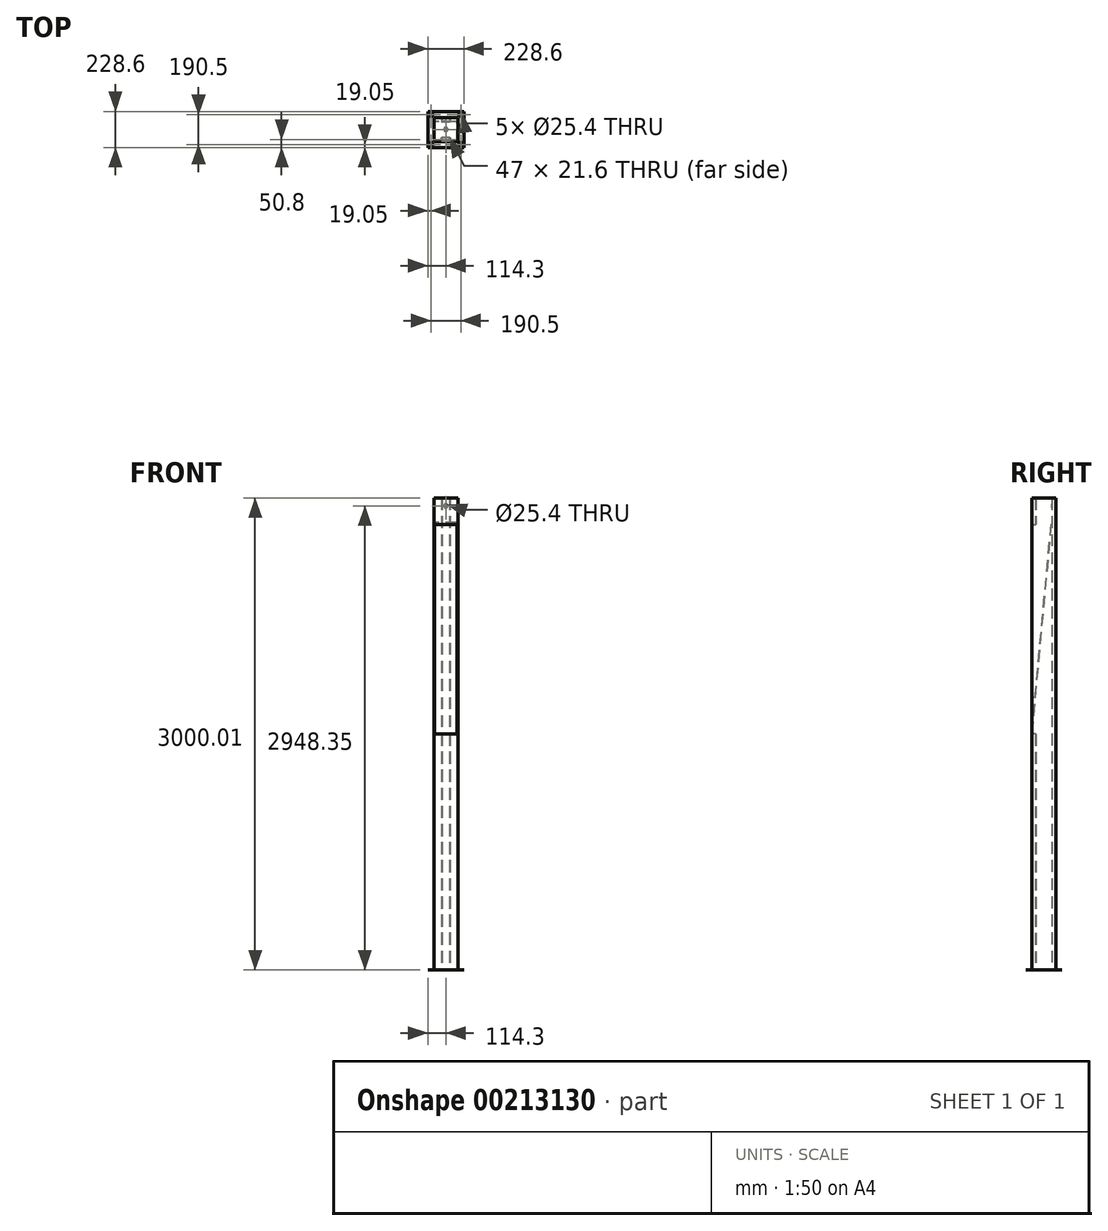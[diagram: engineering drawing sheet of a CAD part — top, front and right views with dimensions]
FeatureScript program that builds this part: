
annotation { "Feature Type Name" : "Feature", "Feature Type Description" : "" }
export const myFeature = defineFeature(function(context is Context, id is Id, definition is map)
    precondition{}
    {
        {
            var Q0;
            Q0=qCreatedBy(makeId("Top.planeOp"),FACE);
            var sketch = newSketch(context, id + "F0", { "sketchPlane" : qUnion([Q0])});
            skPoint(sketch, "E0.middle", {"position": v(0, 0) * mm});
            skLineSegment(sketch, "E1", {"start": v(-76.2, 76.2) * mm, "end": v(-25.4, 76.2) * mm});
            skLineSegment(sketch, "E2", {"start": v(-25.4, 76.2) * mm, "end": v(-25.4, 50.8) * mm});
            skLineSegment(sketch, "E3.MirrorCS", {"start": v(-25.4, -76.2) * mm, "end": v(-25.4, -50.8) * mm});
            skLineSegment(sketch, "E4.MirrorCS", {"start": v(-76.2, -76.2) * mm, "end": v(-25.4, -76.2) * mm});
            skLineSegment(sketch, "E5.0", {"start": v(-27.3, -74.3) * mm, "end": v(-27.3, -50.8) * mm});
            skLineSegment(sketch, "E5.1", {"start": v(-27.3, 74.3) * mm, "end": v(-27.3, 50.8) * mm});
            skLineSegment(sketch, "E5.2", {"start": v(-74.3, 74.3) * mm, "end": v(-27.3, 74.3) * mm});
            skLineSegment(sketch, "E5.3", {"start": v(-74.3, 74.3) * mm, "end": v(-74.3, -74.3) * mm});
            skLineSegment(sketch, "E5.4", {"start": v(-74.3, -74.3) * mm, "end": v(-27.3, -74.3) * mm});
            skLineSegment(sketch, "E6", {"start": v(-27.3, 50.8) * mm, "end": v(-25.4, 50.8) * mm});
            skLineSegment(sketch, "E7", {"start": v(-27.3, -50.8) * mm, "end": v(-25.4, -50.8) * mm});
            skLineSegment(sketch, "E8", {"start": v(-76.2, 76.2) * mm, "end": v(-76.2, -76.2) * mm});
            skLineSegment(sketch, "E9.MirrorCS", {"start": v(25.4, 76.2) * mm, "end": v(25.4, 50.8) * mm});
            skLineSegment(sketch, "E10.MirrorCS", {"start": v(27.3, 74.3) * mm, "end": v(27.3, 50.8) * mm});
            skLineSegment(sketch, "E11.MirrorCS", {"start": v(74.3, 74.3) * mm, "end": v(27.3, 74.3) * mm});
            skLineSegment(sketch, "E12.MirrorCS", {"start": v(74.3, 74.3) * mm, "end": v(74.3, -74.3) * mm});
            skLineSegment(sketch, "E13.MirrorCS", {"start": v(74.3, -74.3) * mm, "end": v(27.3, -74.3) * mm});
            skLineSegment(sketch, "E14.MirrorCS", {"start": v(27.3, -74.3) * mm, "end": v(27.3, -50.8) * mm});
            skLineSegment(sketch, "E15.MirrorCS", {"start": v(25.4, -76.2) * mm, "end": v(25.4, -50.8) * mm});
            skLineSegment(sketch, "E16.MirrorCS", {"start": v(27.3, -50.8) * mm, "end": v(25.4, -50.8) * mm});
            skLineSegment(sketch, "E17.MirrorCS", {"start": v(27.3, 50.8) * mm, "end": v(25.4, 50.8) * mm});
            skLineSegment(sketch, "E18", {"start": v(25.4, -76.2) * mm, "end": v(76.2, -76.2) * mm});
            skLineSegment(sketch, "E19", {"start": v(76.2, -76.2) * mm, "end": v(76.2, 76.2) * mm});
            skLineSegment(sketch, "E20", {"start": v(25.4, 76.2) * mm, "end": v(76.2, 76.2) * mm});
            skLineSegment(sketch, "E21", {"start": v(-25.4, 76.2) * mm, "end": v(25.4, 76.2) * mm});
            skLineSegment(sketch, "E22", {"start": v(-25.4, 50.8) * mm, "end": v(25.4, 50.8) * mm});
            skLineSegment(sketch, "E23.0", {"start": v(-23.5, 74.3) * mm, "end": v(23.5, 74.3) * mm});
            skLineSegment(sketch, "E23.1", {"start": v(-23.5, 74.3) * mm, "end": v(-23.5, 52.7) * mm});
            skLineSegment(sketch, "E23.2", {"start": v(-23.5, 52.7) * mm, "end": v(23.5, 52.7) * mm});
            skLineSegment(sketch, "E23.3", {"start": v(23.5, 74.3) * mm, "end": v(23.5, 52.7) * mm});
            skLineSegment(sketch, "E24.MirrorCS", {"start": v(-25.4, -50.8) * mm, "end": v(25.4, -50.8) * mm});
            skLineSegment(sketch, "E25.MirrorCS", {"start": v(-23.5, -52.7) * mm, "end": v(23.5, -52.7) * mm});
            skLineSegment(sketch, "E26.MirrorCS", {"start": v(-23.5, -74.3) * mm, "end": v(-23.5, -52.7) * mm});
            skLineSegment(sketch, "E27.MirrorCS", {"start": v(-23.5, -74.3) * mm, "end": v(23.5, -74.3) * mm});
            skLineSegment(sketch, "E28.MirrorCS", {"start": v(23.5, -74.3) * mm, "end": v(23.5, -52.7) * mm});
            skLineSegment(sketch, "E29.MirrorCS", {"start": v(-25.4, -76.2) * mm, "end": v(25.4, -76.2) * mm});
            skSolve(sketch);
        }
        {
            var Q0;
            Q0=makeQuery(id+"F0.imprint","IMPRINT",FACE,{"disambiguationData":[TD([[makeQuery(id+"F0.imprint","IMPRINT",EDGE,{"derivedFrom":sQuery(id+"F0.wireOp",EDGE,"E3.MirrorCS")}),-1.0]])]});
            var Q1;
            Q1=makeQuery(id+"F0.imprint","IMPRINT",FACE,{"disambiguationData":[TD([[makeQuery(id+"F0.imprint","IMPRINT",EDGE,{"derivedFrom":sQuery(id+"F0.wireOp",EDGE,"E2")}),1.0]])]});
            var Q2;
            Q2=makeQuery(id+"F0.imprint","IMPRINT",FACE,{"disambiguationData":[TD([[makeQuery(id+"F0.imprint","IMPRINT",EDGE,{"derivedFrom":sQuery(id+"F0.wireOp",EDGE,"E1")}),-1.0]])]});
            var Q3;
            Q3=makeQuery(id+"F0.imprint","IMPRINT",FACE,{"disambiguationData":[TD([[makeQuery(id+"F0.imprint","IMPRINT",EDGE,{"derivedFrom":sQuery(id+"F0.wireOp",EDGE,"E10.MirrorCS")}),-1.0]])]});
            extrude(context, id + "F1", {"entities" : qUnion([Q0, Q1, Q2, Q3]), "endBound" : BoundingType.SYMMETRIC, "depth" : 3000 * mm});
        }
        {
            var Q0;
            Q0=makeQuery(id+"F1.opExtrude","CAP_FACE",FACE,{"disambiguationData":[OSD([sQuery(id+"F0.wireOp",EDGE,"E1"),sQuery(id+"F0.wireOp",EDGE,"E4.MirrorCS"),sQuery(id+"F0.wireOp",EDGE,"E5.0"),sQuery(id+"F0.wireOp",EDGE,"E5.1"),sQuery(id+"F0.wireOp",EDGE,"E5.2"),sQuery(id+"F0.wireOp",EDGE,"E5.3"),sQuery(id+"F0.wireOp",EDGE,"E5.4"),sQuery(id+"F0.wireOp",EDGE,"E6"),sQuery(id+"F0.wireOp",EDGE,"E7"),sQuery(id+"F0.wireOp",EDGE,"E8"),sQuery(id+"F0.wireOp",EDGE,"E10.MirrorCS"),sQuery(id+"F0.wireOp",EDGE,"E11.MirrorCS"),sQuery(id+"F0.wireOp",EDGE,"E12.MirrorCS"),sQuery(id+"F0.wireOp",EDGE,"E13.MirrorCS"),sQuery(id+"F0.wireOp",EDGE,"E14.MirrorCS"),sQuery(id+"F0.wireOp",EDGE,"E16.MirrorCS"),sQuery(id+"F0.wireOp",EDGE,"E17.MirrorCS"),sQuery(id+"F0.wireOp",EDGE,"E18"),sQuery(id+"F0.wireOp",EDGE,"E19"),sQuery(id+"F0.wireOp",EDGE,"E20"),sQuery(id+"F0.wireOp",EDGE,"E21"),sQuery(id+"F0.wireOp",EDGE,"E22"),sQuery(id+"F0.wireOp",EDGE,"E23.0"),sQuery(id+"F0.wireOp",EDGE,"E23.1"),sQuery(id+"F0.wireOp",EDGE,"E23.2"),sQuery(id+"F0.wireOp",EDGE,"E23.3"),sQuery(id+"F0.wireOp",EDGE,"E24.MirrorCS"),sQuery(id+"F0.wireOp",EDGE,"E25.MirrorCS"),sQuery(id+"F0.wireOp",EDGE,"E26.MirrorCS"),sQuery(id+"F0.wireOp",EDGE,"E27.MirrorCS"),sQuery(id+"F0.wireOp",EDGE,"E28.MirrorCS"),sQuery(id+"F0.wireOp",EDGE,"E29.MirrorCS")])],"isStart":true});
            var sketch = newSketch(context, id + "F2", { "sketchPlane" : qUnion([Q0])});
            skLineSegment(sketch, "E30.bottom", {"start": v(-114.3, 114.3) * mm, "end": v(114.3, 114.3) * mm});
            skLineSegment(sketch, "E30.top", {"start": v(-114.3, -114.3) * mm, "end": v(114.3, -114.3) * mm});
            skLineSegment(sketch, "E30.left", {"start": v(-114.3, 114.3) * mm, "end": v(-114.3, -114.3) * mm});
            skLineSegment(sketch, "E30.right", {"start": v(114.3, 114.3) * mm, "end": v(114.3, -114.3) * mm});
            skPoint(sketch, "E30.middle", {"position": v(0, 0) * mm});
            skLineSegment(sketch, "E31", {"start": v(-114.3, 114.3) * mm, "end": v(-76.2, 76.2) * mm, "construction": true});
            skCircle(sketch, "E32", {"center": v(-95.25, 95.25) * mm, "radius": 12.7 * mm});
            skCircle(sketch, "E33.MirrorC", {"center": v(-95.25, -95.25) * mm, "radius": 12.7 * mm});
            skCircle(sketch, "E34.MirrorC", {"center": v(95.25, 95.25) * mm, "radius": 12.7 * mm});
            skCircle(sketch, "E35.MirrorC", {"center": v(95.25, -95.25) * mm, "radius": 12.7 * mm});
            skCircle(sketch, "E36", {"center": v(0, 0) * mm, "radius": 12.7 * mm});
            skLineSegment(sketch, "E37.bottom", {"start": v(-95.25, -95.25) * mm, "end": v(95.25, -95.25) * mm, "construction": true});
            skLineSegment(sketch, "E37.top", {"start": v(-95.25, 95.25) * mm, "end": v(95.25, 95.25) * mm, "construction": true});
            skLineSegment(sketch, "E37.left", {"start": v(-95.25, -95.25) * mm, "end": v(-95.25, 95.25) * mm, "construction": true});
            skLineSegment(sketch, "E37.right", {"start": v(95.25, -95.25) * mm, "end": v(95.25, 95.25) * mm, "construction": true});
            skSolve(sketch);
        }
        {
            var Q0;
            Q0 = qSketchRegion(id + "F2", true);
            extrude(context, id + "F3", {"entities" : qUnion([Q0]), "depth" : 3 / 203.2 * mm});
        }
        {
            var Q0;
            Q0=makeQuery(id+"F1.opExtrude","SWEPT_FACE",FACE,{"disambiguationData":[OSD([sQuery(id+"F0.wireOp",EDGE,"E4.MirrorCS"),sQuery(id+"F0.wireOp",EDGE,"E18"),sQuery(id+"F0.wireOp",EDGE,"E29.MirrorCS")])]});
            var sketch = newSketch(context, id + "F4", { "sketchPlane" : qUnion([Q0])});
            skLineSegment(sketch, "E38", {"start": v(0, 1500) * mm, "end": v(0, 1330) * mm, "construction": true});
            skPoint(sketch, "E38.endSnap0", {"position": v(0, 1500) * mm});
            skLineSegment(sketch, "E39.bottom", {"start": v(72.28, 1330) * mm, "end": v(-72.28, 1330) * mm});
            skLineSegment(sketch, "E39.left", {"start": v(72.28, 1330) * mm, "end": v(72.28, 0) * mm});
            skLineSegment(sketch, "E39.right", {"start": v(-72.28, 1330) * mm, "end": v(-72.28, 0) * mm});
            skPoint(sketch, "E39.middle", {"position": v(0, 0) * mm});
            skLineSegment(sketch, "E40", {"start": v(-72.28, 0) * mm, "end": v(72.28, 0) * mm});
            skPoint(sketch, "E39.top.end.orphan", {"position": v(-72.28, -1330) * mm});
            skPoint(sketch, "E39.top.start.orphan", {"position": v(72.28, -1330) * mm});
            skPoint(sketch, "E41.orphan", {"position": v(76.2, 0) * mm});
            skSolve(sketch);
        }
        {
            var Q0;
            Q0=makeQuery(id+"F4.imprint","IMPRINT",FACE,{"disambiguationData":[TD([[makeQuery(id+"F4.imprint","IMPRINT",EDGE,{"derivedFrom":sQuery(id+"F4.wireOp",EDGE,"E39.bottom")}),1.0]])]});
            extrude(context, id + "F5", {"entities" : qUnion([Q0]), "operationType" : NewBodyOperationType.REMOVE, "oppositeDirection" : true, "depth" : 81 * mm});
        }
        {
            var Q0;
            Q0=makeQuery(id+"F1.opExtrude","CAP_FACE",FACE,{"disambiguationData":[OSD([sQuery(id+"F0.wireOp",EDGE,"E1"),sQuery(id+"F0.wireOp",EDGE,"E4.MirrorCS"),sQuery(id+"F0.wireOp",EDGE,"E5.0"),sQuery(id+"F0.wireOp",EDGE,"E5.1"),sQuery(id+"F0.wireOp",EDGE,"E5.2"),sQuery(id+"F0.wireOp",EDGE,"E5.3"),sQuery(id+"F0.wireOp",EDGE,"E5.4"),sQuery(id+"F0.wireOp",EDGE,"E6"),sQuery(id+"F0.wireOp",EDGE,"E7"),sQuery(id+"F0.wireOp",EDGE,"E8"),sQuery(id+"F0.wireOp",EDGE,"E10.MirrorCS"),sQuery(id+"F0.wireOp",EDGE,"E11.MirrorCS"),sQuery(id+"F0.wireOp",EDGE,"E12.MirrorCS"),sQuery(id+"F0.wireOp",EDGE,"E13.MirrorCS"),sQuery(id+"F0.wireOp",EDGE,"E14.MirrorCS"),sQuery(id+"F0.wireOp",EDGE,"E16.MirrorCS"),sQuery(id+"F0.wireOp",EDGE,"E17.MirrorCS"),sQuery(id+"F0.wireOp",EDGE,"E18"),sQuery(id+"F0.wireOp",EDGE,"E19"),sQuery(id+"F0.wireOp",EDGE,"E20"),sQuery(id+"F0.wireOp",EDGE,"E21"),sQuery(id+"F0.wireOp",EDGE,"E22"),sQuery(id+"F0.wireOp",EDGE,"E23.0"),sQuery(id+"F0.wireOp",EDGE,"E23.1"),sQuery(id+"F0.wireOp",EDGE,"E23.2"),sQuery(id+"F0.wireOp",EDGE,"E23.3"),sQuery(id+"F0.wireOp",EDGE,"E24.MirrorCS"),sQuery(id+"F0.wireOp",EDGE,"E25.MirrorCS"),sQuery(id+"F0.wireOp",EDGE,"E26.MirrorCS"),sQuery(id+"F0.wireOp",EDGE,"E27.MirrorCS"),sQuery(id+"F0.wireOp",EDGE,"E28.MirrorCS"),sQuery(id+"F0.wireOp",EDGE,"E29.MirrorCS")])],"isStart":false});
            var sketch = newSketch(context, id + "F6", { "sketchPlane" : qUnion([Q0])});
            skLineSegment(sketch, "E42.bottom", {"start": v(-76.2, 76.2) * mm, "end": v(76.2, 76.2) * mm});
            skLineSegment(sketch, "E42.top", {"start": v(-76.2, -76.2) * mm, "end": v(76.2, -76.2) * mm});
            skLineSegment(sketch, "E42.left", {"start": v(-76.2, 76.2) * mm, "end": v(-76.2, -76.2) * mm});
            skLineSegment(sketch, "E42.right", {"start": v(76.2, 76.2) * mm, "end": v(76.2, -76.2) * mm});
            skSolve(sketch);
        }
        {
            var Q0;
            Q0 = qSketchRegion(id + "F6", true);
            extrude(context, id + "F7", {"entities" : qUnion([Q0]), "operationType" : NewBodyOperationType.ADD, "oppositeDirection" : true, "depth" : 1.9 * mm});
        }
        {
            var Q0;
            Q0=qCreatedBy(makeId("Right.planeOp"),FACE);
            var sketch = newSketch(context, id + "F8", { "sketchPlane" : qUnion([Q0])});
            skLineSegment(sketch, "E43", {"start": v(-75.2, 0) * mm, "end": v(49.65, 1342.92) * mm, "construction": true});
            skLineSegment(sketch, "E44.0", {"start": v(-74.25, -0.16) * mm, "end": v(50.61, 1343.05) * mm});
            skLineSegment(sketch, "E45.0", {"start": v(-76.14, 0.01) * mm, "end": v(48.72, 1343.23) * mm});
            skLineSegment(sketch, "E46", {"start": v(-76.14, 0.01) * mm, "end": v(-74.25, -0.16) * mm});
            skLineSegment(sketch, "E47", {"start": v(48.72, 1343.23) * mm, "end": v(50.61, 1343.05) * mm});
            skSolve(sketch);
        }
        {
            var Q0;
            Q0 = qSketchRegion(id + "F8", true);
            extrude(context, id + "F9", {"entities" : qUnion([Q0]), "operationType" : NewBodyOperationType.ADD, "endBound" : BoundingType.SYMMETRIC, "depth" : 144.4 * mm});
        }
        {
            var Q0;
            Q0=makeQuery(id+"F1.opExtrude","SWEPT_FACE",FACE,{"disambiguationData":[OSD([sQuery(id+"F0.wireOp",EDGE,"E6"),sQuery(id+"F0.wireOp",EDGE,"E17.MirrorCS"),sQuery(id+"F0.wireOp",EDGE,"E22")])]});
            var sketch = newSketch(context, id + "F10", { "sketchPlane" : qUnion([Q0])});
            skLineSegment(sketch, "E48", {"start": v(0, 1498.1) * mm, "end": v(0, 1448.34) * mm, "construction": true});
            skPoint(sketch, "E48.endSnap0", {"position": v(0, 1498.1) * mm});
            skCircle(sketch, "E49", {"center": v(0, 1448.34) * mm, "radius": 12.7 * mm});
            skSolve(sketch);
        }
        {
            var Q0;
            Q0=makeQuery(id+"F10.imprint","IMPRINT",FACE,{"disambiguationData":[TD([[makeQuery(id+"F10.imprint","IMPRINT",EDGE,{"derivedFrom":sQuery(id+"F10.wireOp",EDGE,"E49")}),1.0]])]});
            extrude(context, id + "F11", {"entities" : qUnion([Q0]), "operationType" : NewBodyOperationType.REMOVE, "endBound" : BoundingType.UP_TO_NEXT, "oppositeDirection" : true, "depth" : 25 * mm});
        }
    });
